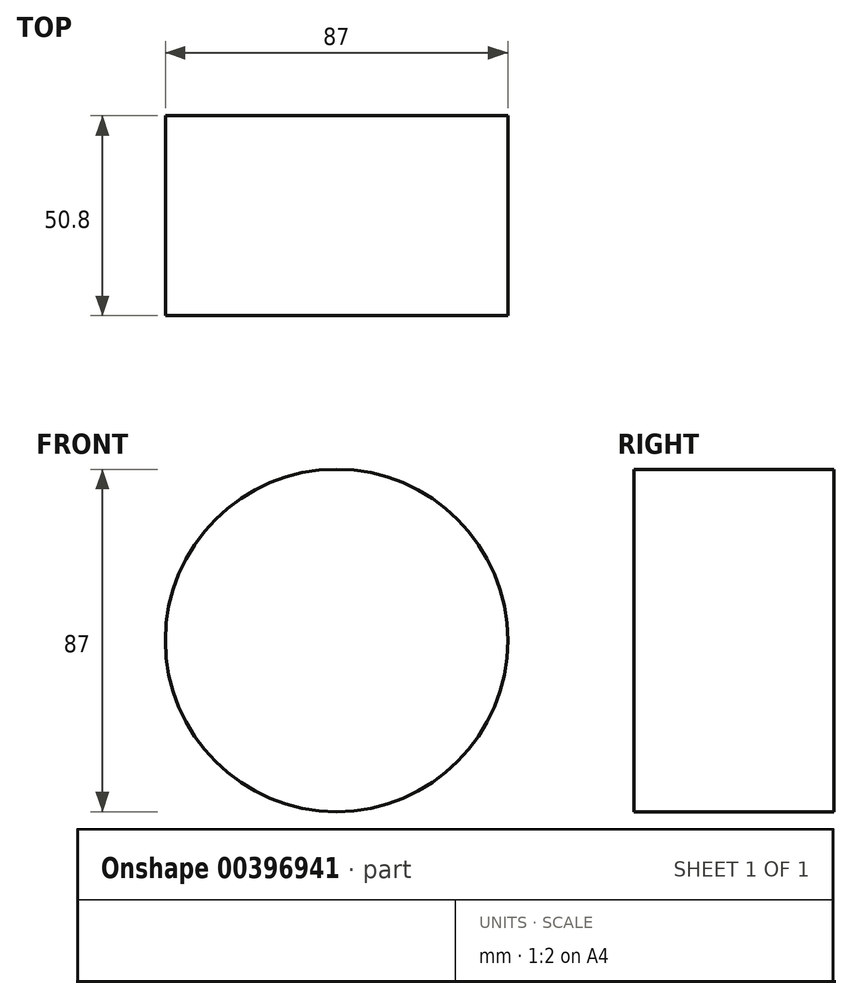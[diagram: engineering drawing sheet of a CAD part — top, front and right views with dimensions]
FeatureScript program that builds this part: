
annotation { "Feature Type Name" : "Feature", "Feature Type Description" : "" }
export const myFeature = defineFeature(function(context is Context, id is Id, definition is map)
    precondition{}
    {
        {
            var Q0;
            Q0=qCreatedBy(makeId("Front.planeOp"),FACE);
            var sketch = newSketch(context, id + "F0", { "sketchPlane" : qUnion([Q0])});
            skCircle(sketch, "E0", {"center": v(0, 0) * mm, "radius": 43.5 * mm});
            skSolve(sketch);
        }
        {
            var Q0;
            Q0 = qConstructionFilter(qBodyType(qCreatedBy(id + "F0" ,EDGE), BodyType.WIRE), ConstructionObject.NO);
            extrude(context, id + "F1", {"bodyType" : ToolBodyType.SURFACE, "surfaceEntities" : qUnion([Q0]), "depth" : 50.8 * mm});
        }
    });
